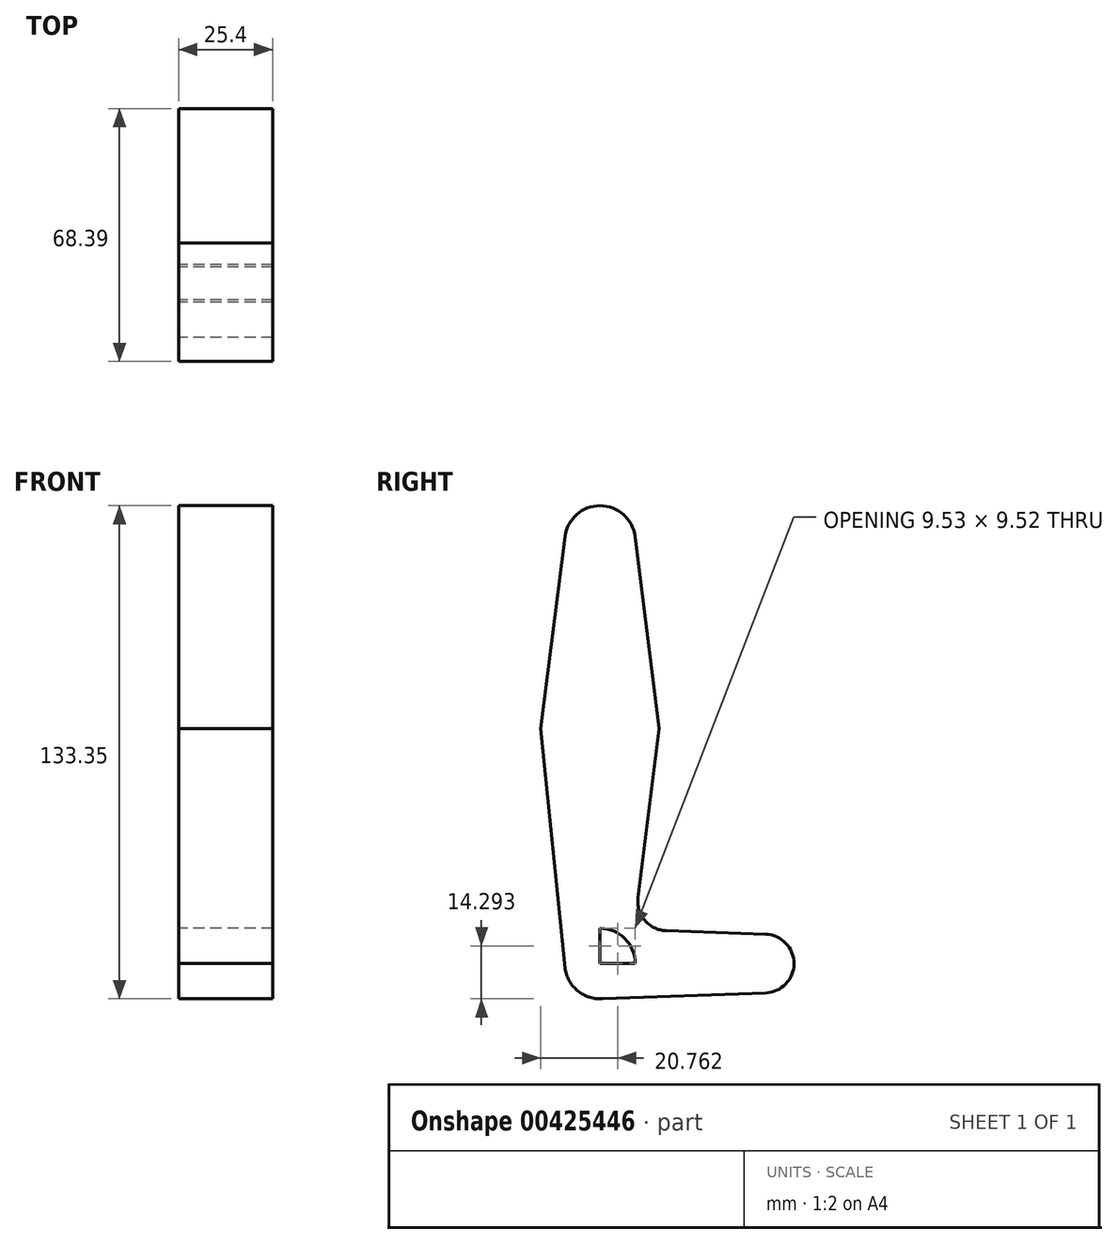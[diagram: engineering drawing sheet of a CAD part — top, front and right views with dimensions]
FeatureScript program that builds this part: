
annotation { "Feature Type Name" : "Feature", "Feature Type Description" : "" }
export const myFeature = defineFeature(function(context is Context, id is Id, definition is map)
    precondition{}
    {
        {
            var Q0;
            Q0=qCreatedBy(makeId("Right.planeOp"),FACE);
            var sketch = newSketch(context, id + "F0", { "sketchPlane" : qUnion([Q0])});
            skLineSegment(sketch, "E0", {"start": v(0, 50.8) * mm, "end": v(0, -63.5) * mm});
            skLineSegment(sketch, "E1", {"start": v(0, -63.5) * mm, "end": v(44.45, -63.5) * mm});
            skCircle(sketch, "E2", {"center": v(0, 50.8) * mm, "radius": 9.53 * mm});
            skCircle(sketch, "E3", {"center": v(0, 0) * mm, "radius": 15.88 * mm});
            skCircle(sketch, "E4", {"center": v(0, -63.5) * mm, "radius": 9.53 * mm});
            skCircle(sketch, "E5", {"center": v(44.45, -63.5) * mm, "radius": 7.94 * mm});
            skLineSegment(sketch, "E6", {"start": v(-9.45, 52) * mm, "end": v(-16, 0) * mm});
            skLineSegment(sketch, "E7", {"start": v(-16, 0) * mm, "end": v(-9.52, -63.5) * mm});
            skLineSegment(sketch, "E8", {"start": v(9.45, 52) * mm, "end": v(16, 0) * mm});
            skLineSegment(sketch, "E9", {"start": v(16, 0) * mm, "end": v(10.25, -45.67) * mm});
            skLineSegment(sketch, "E10", {"start": v(17.85, -54.6) * mm, "end": v(44.73, -55.57) * mm});
            skLineSegment(sketch, "E11", {"start": v(0, -73.02) * mm, "end": v(44.73, -71.43) * mm});
            skArc(sketch, "E12.filletArc", {"start": v(10.25, -45.67) * mm, "mid": v(12.08, -51.81) * mm, "end": v(17.85, -54.6) * mm});
            skSolve(sketch);
        }
        {
            var Q0;
            Q0 = qSketchRegion(id + "F0", true);
            extrude(context, id + "F1", {"entities" : qUnion([Q0]), "depth" : 25.4 * mm});
        }
    });
